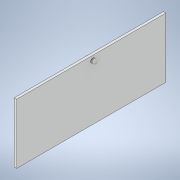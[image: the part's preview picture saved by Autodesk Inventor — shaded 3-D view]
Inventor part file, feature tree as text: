
AUTODESK INVENTOR PART (.ipt)
format: ipt  version: 2021 (Build 250183000, 183)  size: 104,960 bytes
history: imported  units: in
note: dims shown in document units (in); Inventor stores cm internally (conversion verified against a paired STEP export)
features: imported_body x1
ambient origin geometry x8: Origin, YZ Plane, XZ Plane, XY Plane, X Axis, Y Axis, Z Axis, Center Point
bodies: Solid1 (imported_parasolid), Body1 (imported_parasolid)
feature tree (1):
  imported_body  NMx_Import_Brep_tag  [imported B-rep: ~12 faces, bbox_mm=[45.0, 820.0, 2040.0]]
